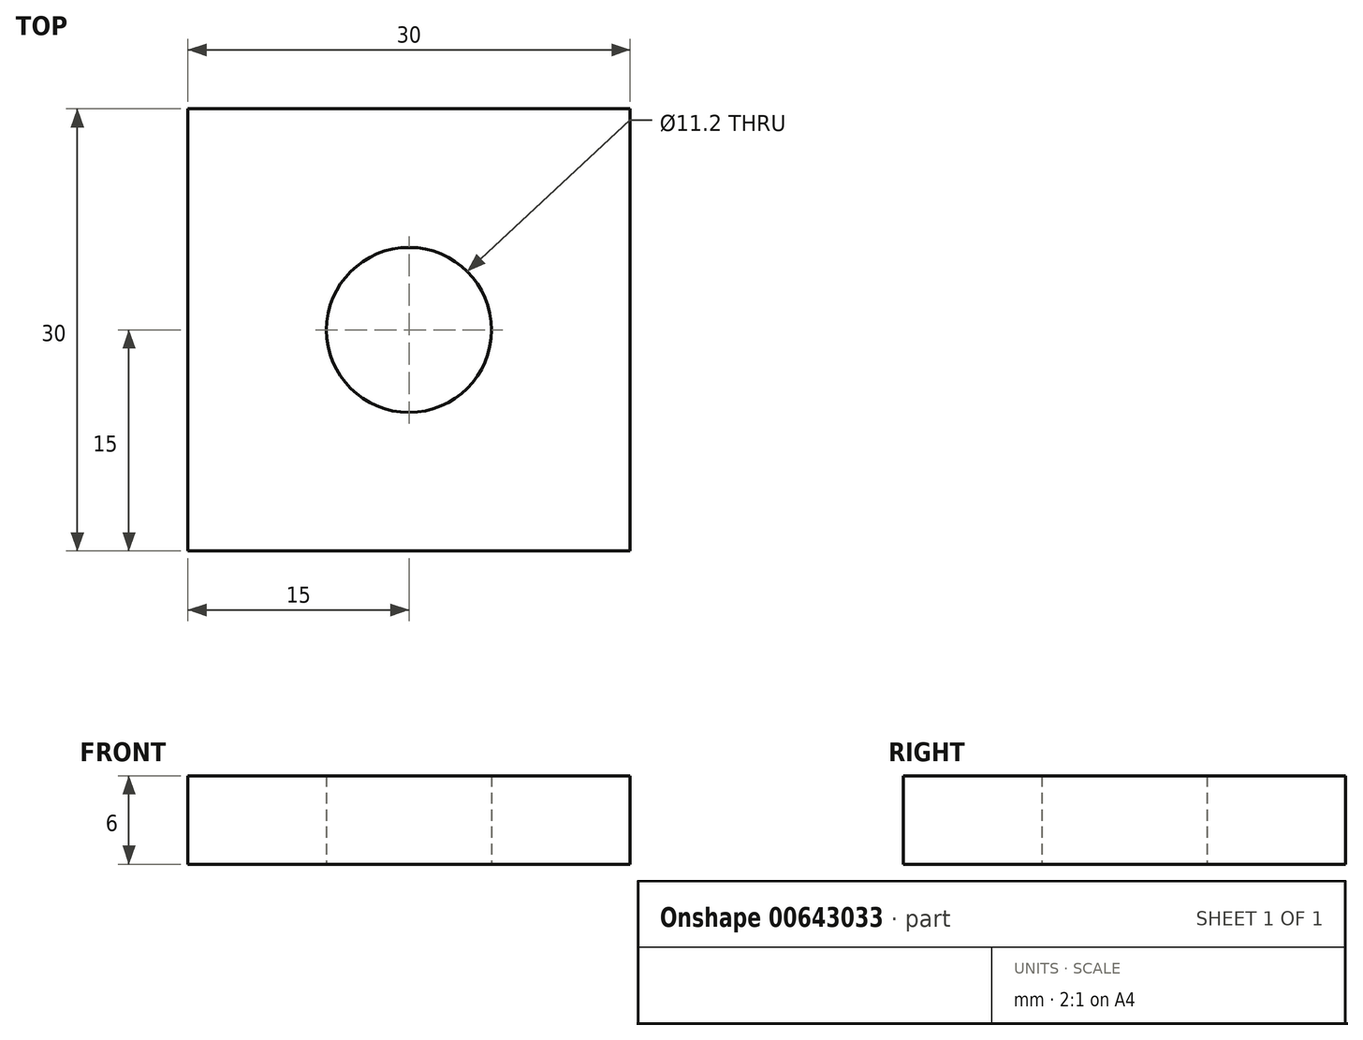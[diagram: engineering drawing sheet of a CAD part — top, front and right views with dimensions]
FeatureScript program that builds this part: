
annotation { "Feature Type Name" : "Feature", "Feature Type Description" : "" }
export const myFeature = defineFeature(function(context is Context, id is Id, definition is map)
    precondition{}
    {
        {
            var Q0;
            Q0=qCreatedBy(makeId("Top.planeOp"),FACE);
            var sketch = newSketch(context, id + "F0", { "sketchPlane" : qUnion([Q0])});
            skLineSegment(sketch, "E0.bottom", {"start": v(15, 15) * mm, "end": v(-15, 15) * mm});
            skLineSegment(sketch, "E0.top", {"start": v(15, -15) * mm, "end": v(-15, -15) * mm});
            skLineSegment(sketch, "E0.left", {"start": v(15, 15) * mm, "end": v(15, -15) * mm});
            skLineSegment(sketch, "E0.right", {"start": v(-15, 15) * mm, "end": v(-15, -15) * mm});
            skPoint(sketch, "E0.middle", {"position": v(0, 0) * mm});
            skCircle(sketch, "E1", {"center": v(0, 0) * mm, "radius": 5.6 * mm});
            skSolve(sketch);
        }
        {
            var Q0;
            Q0=makeQuery(id+"F0.imprint","IMPRINT",FACE,{"disambiguationData":[TD([[makeQuery(id+"F0.imprint","IMPRINT",EDGE,{"derivedFrom":sQuery(id+"F0.wireOp",EDGE,"E0.bottom")}),1.0]])]});
            extrude(context, id + "F1", {"entities" : qUnion([Q0]), "depth" : 6 * mm, "offsetDistance" : 25 * mm});
        }
    });
